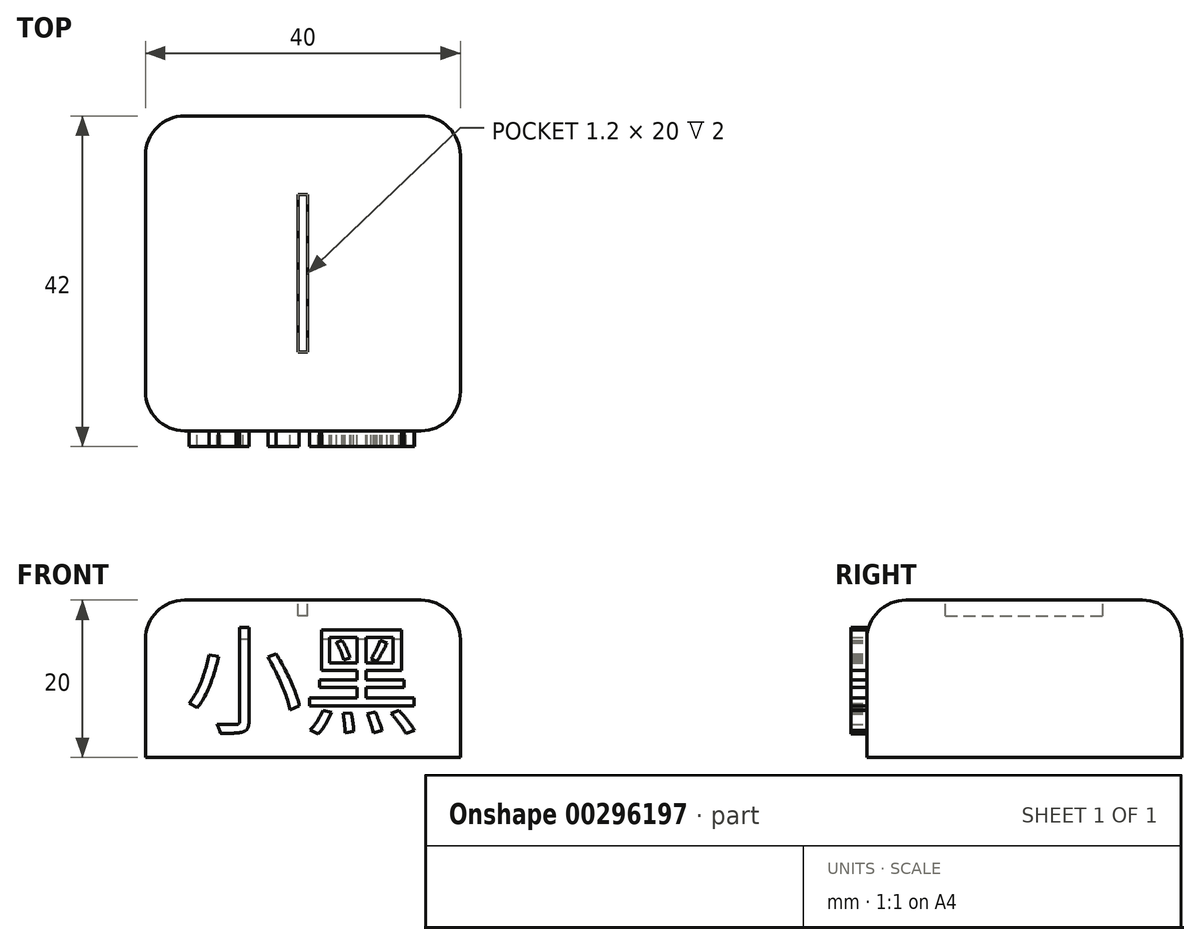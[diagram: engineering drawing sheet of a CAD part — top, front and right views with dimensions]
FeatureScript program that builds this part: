
annotation { "Feature Type Name" : "Feature", "Feature Type Description" : "" }
export const myFeature = defineFeature(function(context is Context, id is Id, definition is map)
    precondition{}
    {
        {
            var Q0;
            Q0=qCreatedBy(makeId("Top.planeOp"),FACE);
            var sketch = newSketch(context, id + "F0", { "sketchPlane" : qUnion([Q0])});
            skLineSegment(sketch, "E0.bottom", {"start": v(20, -20) * mm, "end": v(-20, -20) * mm});
            skLineSegment(sketch, "E0.top", {"start": v(20, 20) * mm, "end": v(-20, 20) * mm});
            skLineSegment(sketch, "E0.left", {"start": v(20, -20) * mm, "end": v(20, 20) * mm});
            skLineSegment(sketch, "E0.right", {"start": v(-20, -20) * mm, "end": v(-20, 20) * mm});
            skPoint(sketch, "E0.middle", {"position": v(0, 0) * mm});
            skLineSegment(sketch, "E1.bottom", {"start": v(0.6, -10) * mm, "end": v(-0.6, -10) * mm});
            skLineSegment(sketch, "E1.top", {"start": v(0.6, 10) * mm, "end": v(-0.6, 10) * mm});
            skLineSegment(sketch, "E1.left", {"start": v(0.6, -10) * mm, "end": v(0.6, 10) * mm});
            skLineSegment(sketch, "E1.right", {"start": v(-0.6, -10) * mm, "end": v(-0.6, 10) * mm});
            skSolve(sketch);
        }
        {
            var Q0;
            Q0=makeQuery(id+"F0.imprint","IMPRINT",FACE,{"disambiguationData":[TD([[makeQuery(id+"F0.imprint","IMPRINT",EDGE,{"derivedFrom":sQuery(id+"F0.wireOp",EDGE,"E0.bottom")}),-1.0]])]});
            var Q1;
            Q1=makeQuery(id+"F0.imprint","IMPRINT",FACE,{"disambiguationData":[TD([[makeQuery(id+"F0.imprint","IMPRINT",EDGE,{"derivedFrom":sQuery(id+"F0.wireOp",EDGE,"E1.bottom")}),-1.0]])]});
            extrude(context, id + "F1", {"entities" : qUnion([Q0, Q1]), "oppositeDirection" : true, "depth" : 20 * mm});
        }
        {
            var Q0;
            Q0=makeQuery(id+"F0.imprint","IMPRINT",FACE,{"disambiguationData":[TD([[makeQuery(id+"F0.imprint","IMPRINT",EDGE,{"derivedFrom":sQuery(id+"F0.wireOp",EDGE,"E1.bottom")}),-1.0]])]});
            extrude(context, id + "F2", {"entities" : qUnion([Q0]), "operationType" : NewBodyOperationType.REMOVE, "oppositeDirection" : true, "depth" : 2 * mm});
        }
        {
            var Q0;
            Q0=makeQuery(id+"F2.boolean.opBoolean","COPY",EDGE,{"derivedFrom":makeQuery(id+"F2.opExtrude","CAP_EDGE",EDGE,{"disambiguationData":[OSD([sQuery(id+"F0.wireOp",EDGE,"E1.left")])],"isStart":true})});
            var Q1;
            Q1=makeQuery(id+"F2.boolean.opBoolean","COPY",EDGE,{"derivedFrom":makeQuery(id+"F2.opExtrude","CAP_EDGE",EDGE,{"disambiguationData":[OSD([sQuery(id+"F0.wireOp",EDGE,"E1.right")])],"isStart":true})});
            var Q2;
            Q2=makeQuery(id+"F1.opExtrude","SWEPT_EDGE",EDGE,{"disambiguationData":[OSD([sQuery(id+"F0.wireOp",EDGE,"E0.bottom"),sQuery(id+"F0.wireOp",EDGE,"E0.left")])]});
            var Q3;
            Q3=makeQuery(id+"F1.opExtrude","SWEPT_EDGE",EDGE,{"disambiguationData":[OSD([sQuery(id+"F0.wireOp",EDGE,"E0.top"),sQuery(id+"F0.wireOp",EDGE,"E0.left")])]});
            var Q4;
            Q4=makeQuery(id+"F1.opExtrude","CAP_EDGE",EDGE,{"disambiguationData":[OSD([sQuery(id+"F0.wireOp",EDGE,"E0.left")])],"isStart":true});
            var Q5;
            Q5=makeQuery(id+"F1.opExtrude","SWEPT_EDGE",EDGE,{"disambiguationData":[OSD([sQuery(id+"F0.wireOp",EDGE,"E0.bottom"),sQuery(id+"F0.wireOp",EDGE,"E0.right")])]});
            var Q6;
            Q6=makeQuery(id+"F1.opExtrude","SWEPT_EDGE",EDGE,{"disambiguationData":[OSD([sQuery(id+"F0.wireOp",EDGE,"E0.top"),sQuery(id+"F0.wireOp",EDGE,"E0.right")])]});
            var Q7;
            Q7=makeQuery(id+"F1.opExtrude","CAP_EDGE",EDGE,{"disambiguationData":[OSD([sQuery(id+"F0.wireOp",EDGE,"E0.top")])],"isStart":true});
            var Q8;
            Q8=makeQuery(id+"F1.opExtrude","CAP_EDGE",EDGE,{"disambiguationData":[OSD([sQuery(id+"F0.wireOp",EDGE,"E0.right")])],"isStart":true});
            var Q9;
            Q9=makeQuery(id+"F1.opExtrude","CAP_EDGE",EDGE,{"disambiguationData":[OSD([sQuery(id+"F0.wireOp",EDGE,"E0.bottom")])],"isStart":true});
            fillet(context, id + "F3", {"entities" : qUnion([Q0, Q1, Q2, Q3, Q4, Q5, Q6, Q7, Q8, Q9]), "radius" : 5 * mm, "tangentPropagation" : true, "allowEdgeOverflow" : false});
        }
        {
            var Q0;
            Q0=makeQuery(id+"F1.opExtrude","SWEPT_FACE",FACE,{"disambiguationData":[OSD([sQuery(id+"F0.wireOp",EDGE,"E0.bottom")])]});
            var sketch = newSketch(context, id + "F4", { "sketchPlane" : qUnion([Q0])});
            skText(sketch, "E2", { "text": "小黑", "fontName": "NotoSansCJKtc-Regular.otf"});
            const initialGuessF4  = {"E2": [-0.015, -0.01579, 1, 0, 0.01079]};
            skSetInitialGuess(sketch, initialGuessF4);
            skSolve(sketch);
        }
        {
            var Q0;
            {var subQ0=sQuery(id+"F4.wireOp",EDGE,"E2.sketch_text.stroke-7");Q0=makeQuery(id+"F4.imprint","IMPRINT",FACE,{"disambiguationData":[TD([[makeQuery(id+"F4.imprint","IMPRINT",EDGE,{"derivedFrom":subQ0}),1.0]])]});}
            var Q1;
            {var subQ0=sQuery(id+"F4.wireOp",EDGE,"E2.sketch_text.stroke-1");Q1=makeQuery(id+"F4.imprint","IMPRINT",FACE,{"disambiguationData":[TD([[makeQuery(id+"F4.imprint","IMPRINT",EDGE,{"derivedFrom":subQ0}),1.0]])]});}
            var Q2;
            Q2=makeQuery(id+"F4.imprint","IMPRINT",FACE,{"disambiguationData":[TD([[makeQuery(id+"F4.imprint","IMPRINT",EDGE,{"derivedFrom":sQuery(id+"F4.wireOp",EDGE,"E2.sketch_text.stroke-12")}),1.0]])]});
            var Q3;
            Q3=makeQuery(id+"F4.imprint","IMPRINT",FACE,{"disambiguationData":[TD([[makeQuery(id+"F4.imprint","IMPRINT",EDGE,{"derivedFrom":sQuery(id+"F4.wireOp",EDGE,"E2.sketch_text.stroke-8")}),1.0]])]});
            var Q4;
            {var subQ10=sQuery(id+"F4.wireOp",EDGE,"E2.sketch_text.stroke-25");Q4=makeQuery(id+"F4.imprint","IMPRINT",FACE,{"disambiguationData":[TD([[makeQuery(id+"F4.imprint","IMPRINT",EDGE,{"derivedFrom":subQ10}),1.0]])]});}
            var Q5;
            Q5=makeQuery(id+"F4.imprint","IMPRINT",FACE,{"disambiguationData":[TD([[makeQuery(id+"F4.imprint","IMPRINT",EDGE,{"derivedFrom":sQuery(id+"F4.wireOp",EDGE,"E2.sketch_text.stroke-20")}),1.0]])]});
            var Q6;
            Q6=makeQuery(id+"F4.imprint","IMPRINT",FACE,{"disambiguationData":[TD([[makeQuery(id+"F4.imprint","IMPRINT",EDGE,{"derivedFrom":sQuery(id+"F4.wireOp",EDGE,"E2.sketch_text.stroke-16")}),1.0]])]});
            var Q7;
            {var subQ7=sQuery(id+"F4.wireOp",EDGE,"E2.sketch_text.stroke-27");Q7=makeQuery(id+"F4.imprint","IMPRINT",FACE,{"disambiguationData":[TD([[makeQuery(id+"F4.imprint","IMPRINT",EDGE,{"derivedFrom":subQ7}),1.0]])]});}
            var Q8;
            Q8=makeQuery(id+"F4.imprint","IMPRINT",FACE,{"disambiguationData":[TD([[makeQuery(id+"F4.imprint","IMPRINT",EDGE,{"derivedFrom":sQuery(id+"F4.wireOp",EDGE,"E2.sketch_text.stroke-52")}),1.0]])]});
            var Q9;
            Q9=makeQuery(id+"F4.imprint","IMPRINT",FACE,{"disambiguationData":[TD([[makeQuery(id+"F4.imprint","IMPRINT",EDGE,{"derivedFrom":sQuery(id+"F4.wireOp",EDGE,"E2.sketch_text.stroke-56")}),1.0]])]});
            var Q10;
            Q10=makeQuery(id+"F4.imprint","IMPRINT",FACE,{"disambiguationData":[TD([[makeQuery(id+"F4.imprint","IMPRINT",EDGE,{"derivedFrom":sQuery(id+"F4.wireOp",EDGE,"E2.sketch_text.stroke-60")}),1.0]])]});
            var Q11;
            Q11=makeQuery(id+"F4.imprint","IMPRINT",FACE,{"disambiguationData":[TD([[makeQuery(id+"F4.imprint","IMPRINT",EDGE,{"derivedFrom":sQuery(id+"F4.wireOp",EDGE,"E2.sketch_text.stroke-64")}),1.0]])]});
            extrude(context, id + "F5", {"entities" : qUnion([Q0, Q1, Q2, Q3, Q4, Q5, Q6, Q7, Q8, Q9, Q10, Q11]), "operationType" : NewBodyOperationType.ADD, "depth" : 2 * mm});
        }
    });
